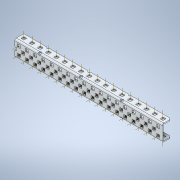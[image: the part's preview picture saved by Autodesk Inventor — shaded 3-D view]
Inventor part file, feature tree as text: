
AUTODESK INVENTOR PART (.ipt)
format: ipt  version: 2020 (Build 240168000, 168)  size: 1,359,872 bytes
history: native  units: in
note: dims shown in document units (in); Inventor stores cm internally (conversion verified against a paired STEP export)
features: other x93, plane x9, pattern_linear x4, split x4, sheet_metal_op x1
ambient origin geometry x8: Origin, YZ Plane, XZ Plane, XY Plane, X Axis, Y Axis, Z Axis, Center Point
bodies: Solid1 (feature_tree)
feature tree (111):
  other  "Work Axis1"
  pattern_linear  "Rectangular Pattern1"  Count1=18 Spacing1=0.5in
  other  "Work Axis72"
  pattern_linear  "Rectangular Pattern2"  Count1=18 Spacing1=0.5in
  pattern_linear  "Rectangular Pattern3"  Count1=18 Spacing1=0.5in
  other  "Work Axis141"
  pattern_linear  "Rectangular Pattern4"  Count1=17 Spacing1=0.5in
  plane  "Work Plane7"
  split  "Split1"
  plane  "Work Plane8"
  split  "Split2"
  split  "Split3"
  plane  "Work Plane9"
  split  "Split4"
  plane  "Work Plane1"
  plane  "Work Plane2"
  other  "Work Point1"
  other  "Work Axis2"
  other  "Work Axis3"
  other  "Work Axis4"
  other  "Work Axis5"
  other  "Work Axis6"
  other  "Work Axis7"
  other  "Work Axis8"
  other  "Work Axis9"
  other  "Work Axis10"
  other  "Work Axis11"
  other  "Work Axis12"
  other  "Work Axis13"
  other  "Work Axis14"
  other  "Work Axis15"
  other  "Work Axis16"
  other  "Work Axis17"
  other  "Work Axis18"
  other  "Work Axis36"
  other  "Work Axis37"
  other  "Work Axis38"
  other  "Work Axis39"
  other  "Work Axis40"
  other  "Work Axis41"
  other  "Work Axis42"
  other  "Work Axis43"
  other  "Work Axis44"
  other  "Work Axis45"
  other  "Work Axis46"
  other  "Work Axis47"
  other  "Work Axis48"
  other  "Work Axis49"
  other  "Work Axis50"
  other  "Work Axis51"
  other  "Work Axis52"
  other  "Work Axis53"
  plane  "Work Plane3"
  plane  "Work Plane4"
  other  "Work Point2"
  other  "Work Axis71"
  other  "Work Point3"
  other  "Work Axis73"
  other  "Work Axis74"
  other  "Work Axis75"
  other  "Work Axis76"
  other  "Work Axis77"
  other  "Work Axis78"
  other  "Work Axis79"
  other  "Work Axis80"
  other  "Work Axis81"
  other  "Work Axis82"
  other  "Work Axis83"
  other  "Work Axis84"
  other  "Work Axis85"
  other  "Work Axis86"
  other  "Work Axis87"
  other  "Work Axis88"
  other  "Work Axis89"
  other  "Work Axis107"
  other  "Work Axis108"
  other  "Work Axis109"
  other  "Work Axis110"
  other  "Work Axis111"
  other  "Work Axis112"
  other  "Work Axis113"
  other  "Work Axis114"
  other  "Work Axis115"
  other  "Work Axis116"
  other  "Work Axis117"
  other  "Work Axis118"
  other  "Work Axis119"
  other  "Work Axis120"
  other  "Work Axis121"
  other  "Work Axis122"
  other  "Work Axis123"
  plane  "Work Plane5"
  plane  "Work Plane6"
  other  "Work Point4"
  other  "Work Axis142"
  other  "Work Axis143"
  other  "Work Axis144"
  other  "Work Axis145"
  other  "Work Axis146"
  other  "Work Axis147"
  other  "Work Axis148"
  other  "Work Axis149"
  other  "Work Axis150"
  other  "Work Axis151"
  other  "Work Axis152"
  other  "Work Axis153"
  other  "Work Axis154"
  other  "Work Axis155"
  other  "Work Axis156"
  other  "Work Axis157"
  sheet_metal_op  "Fold1"
